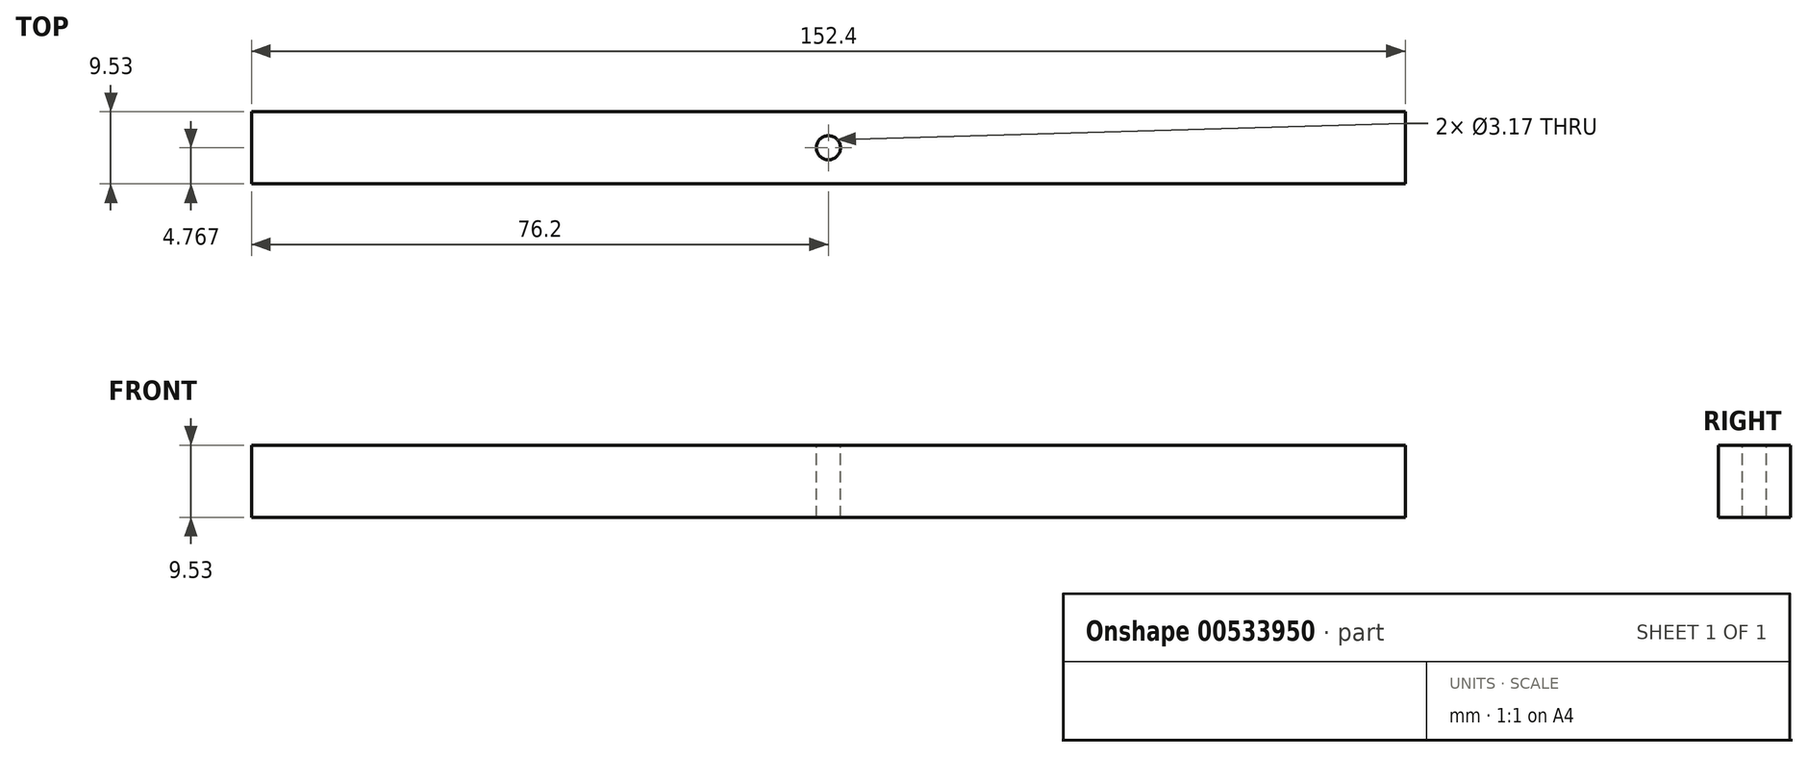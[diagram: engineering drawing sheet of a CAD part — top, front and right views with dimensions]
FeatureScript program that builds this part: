
annotation { "Feature Type Name" : "Feature", "Feature Type Description" : "" }
export const myFeature = defineFeature(function(context is Context, id is Id, definition is map)
    precondition{}
    {
        {
            var Q0;
            Q0=qCreatedBy(makeId("Top.planeOp"),FACE);
            var sketch = newSketch(context, id + "F0", { "sketchPlane" : qUnion([Q0])});
            skLineSegment(sketch, "E0.bottom", {"start": v(0, 0) * mm, "end": v(-152.4, 0) * mm});
            skLineSegment(sketch, "E0.top", {"start": v(0, -9.52) * mm, "end": v(-152.4, -9.53) * mm});
            skLineSegment(sketch, "E0.left", {"start": v(0, 0) * mm, "end": v(0, -9.52) * mm});
            skLineSegment(sketch, "E0.right", {"start": v(-152.4, 0) * mm, "end": v(-152.4, -9.53) * mm});
            skSolve(sketch);
        }
        {
            var Q0;
            Q0 = qSketchRegion(id + "F0", true);
            extrude(context, id + "F1", {"entities" : qUnion([Q0]), "depth" : 9.52 * mm, "offsetDistance" : 25.4 * mm});
        }
        {
            var Q0;
            Q0=makeQuery(id+"F1.opExtrude","CAP_FACE",FACE,{"disambiguationData":[OSD([sQuery(id+"F0.wireOp",EDGE,"E0.bottom"),sQuery(id+"F0.wireOp",EDGE,"E0.top"),sQuery(id+"F0.wireOp",EDGE,"E0.left"),sQuery(id+"F0.wireOp",EDGE,"E0.right")])],"isStart":false});
            var sketch = newSketch(context, id + "F2", { "sketchPlane" : qUnion([Q0])});
            skCircle(sketch, "E1", {"center": v(-76.2, -4.76) * mm, "radius": 1.59 * mm});
            skPoint(sketch, "E1.centerSnap0", {"position": v(0, -4.76) * mm});
            skPoint(sketch, "E1.centerSnap1", {"position": v(-76.2, -9.53) * mm});
            skSolve(sketch);
        }
        {
            var Q0;
            Q0=makeQuery(id+"F2.imprint","IMPRINT",FACE,{"disambiguationData":[TD([[makeQuery(id+"F2.imprint","IMPRINT",EDGE,{"derivedFrom":sQuery(id+"F2.wireOp",EDGE,"E1")}),1.0]])]});
            extrude(context, id + "F3", {"entities" : qUnion([Q0]), "operationType" : NewBodyOperationType.REMOVE, "oppositeDirection" : true, "depth" : 25.4 * mm, "offsetDistance" : 25.4 * mm});
        }
    });
